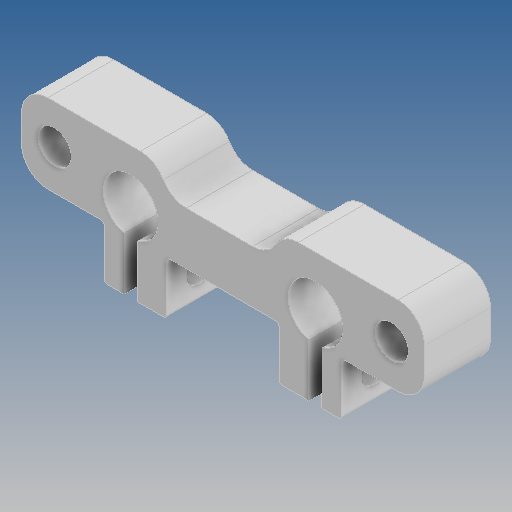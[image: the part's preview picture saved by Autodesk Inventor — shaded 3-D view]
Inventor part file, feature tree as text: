
AUTODESK INVENTOR PART (.ipt)
format: ipt  version: 2020 (Build 240168000, 168)  size: 240,640 bytes
history: native  units: mm
features: sketch x3, extrude x2, fillet x2, hole x1
ambient origin geometry x8: Origin, YZ Plane, XZ Plane, XY Plane, X Axis, Y Axis, Z Axis, Center Point
bodies: Solid1 (feature_tree)
feature tree (8):
  extrude  "Extrusion1"  Depth=28.0mm
  sketch  "Sketch2"  dims[d2=2.0mm d4=2.0mm d6=41.084393mm]
  hole  "Hole1"  [1 undecoded]
  fillet  "Fillet2"  Radius=41.084393mm
  extrude  "Extrusion2"  Depth=12.0mm
  fillet  "Fillet3"  Radius=20.0mm
  sketch  "Sketch1"  dims[d0=8.3mm d1=28.0mm]
  sketch  "Sketch4"  dims[d7=8.0mm d8=12.0mm d9=20.0mm d10=3.0mm d11=3.0mm d13=8.0mm d15=5.5mm d16=5.5mm d17=4.0mm d18=4.0mm d19=10.0mm d20=0.0mm d22=3.5mm d23=6.0mm d24=0.5mm d25=4.0mm d26=6.0mm d27=4.0mm d28=2.0mm d29=90.0deg d30=8.0mm d31=20.594885mm d32=10.0mm d33=5.0mm d34=0.0mm d35=0.0mm d36=0.0mm d37=0.0mm d38=10.0mm d39=0.0mm d40=4.0mm]
note: 1 required parameter value undecoded (feature->parameter linkage not recoverable at this tier; creation-order binding heuristic only, values carry confidence <= 0.55)
